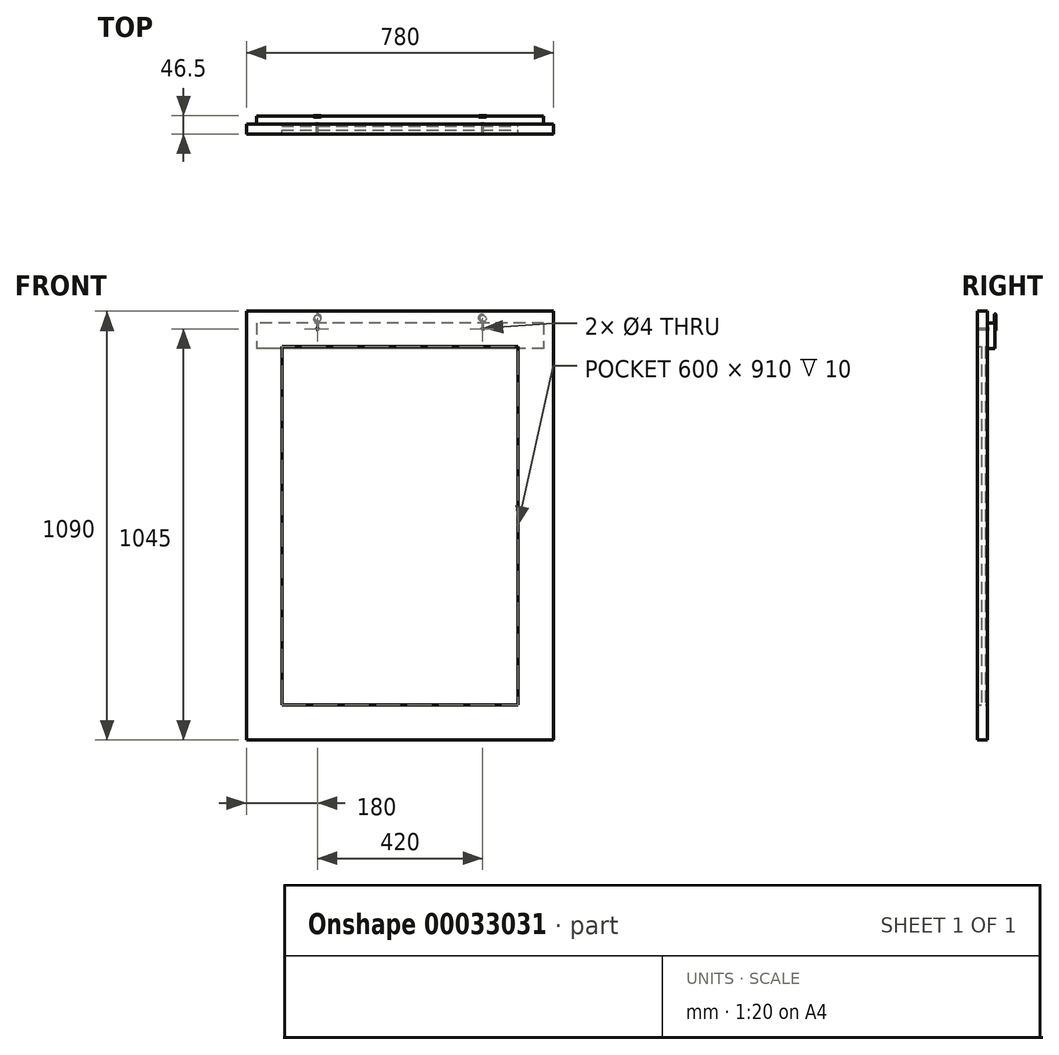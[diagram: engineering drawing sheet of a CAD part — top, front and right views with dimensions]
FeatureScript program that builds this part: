
annotation { "Feature Type Name" : "Feature", "Feature Type Description" : "" }
export const myFeature = defineFeature(function(context is Context, id is Id, definition is map)
    precondition{}
    {
        {
            var Q0;
            Q0=qCreatedBy(makeId("Front.planeOp"),FACE);
            var sketch = newSketch(context, id + "F0", { "sketchPlane" : qUnion([Q0])});
            skLineSegment(sketch, "E0.bottom", {"start": v(-390, 0) * mm, "end": v(390, 0) * mm});
            skLineSegment(sketch, "E0.top", {"start": v(-390, -1090) * mm, "end": v(390, -1090) * mm});
            skLineSegment(sketch, "E0.left", {"start": v(-390, 0) * mm, "end": v(-390, -1090) * mm});
            skLineSegment(sketch, "E0.right", {"start": v(390, 0) * mm, "end": v(390, -1090) * mm});
            skLineSegment(sketch, "E1.0", {"start": v(-300, -90) * mm, "end": v(300, -90) * mm});
            skLineSegment(sketch, "E1.1", {"start": v(-300, -90) * mm, "end": v(-300, -1000) * mm});
            skLineSegment(sketch, "E1.2", {"start": v(-300, -1000) * mm, "end": v(300, -1000) * mm});
            skLineSegment(sketch, "E1.3", {"start": v(300, -90) * mm, "end": v(300, -1000) * mm});
            skSolve(sketch);
        }
        {
            var Q0;
            Q0 = qSketchRegion(id + "F0", true);
            extrude(context, id + "F1", {"entities" : qUnion([Q0]), "depth" : 25 * mm});
        }
        {
            var Q0;
            Q0=qCreatedBy(makeId("Front.planeOp"),FACE);
            cPlane(context, id + "F2", {"entities" : qUnion([Q0]), "cplaneType" : CPlaneType.OFFSET, "offset" : 5 * mm, "width" : 150 * mm, "height" : 150 * mm});
        }
        {
            var Q0;
            Q0=qCreatedBy(id+"F2.planeOp",FACE);
            var sketch = newSketch(context, id + "F3", { "sketchPlane" : qUnion([Q0])});
            skLineSegment(sketch, "E2.0", {"start": v(-300, -90) * mm, "end": v(300, -90) * mm});
            skLineSegment(sketch, "E2.1", {"start": v(-300, -90) * mm, "end": v(-300, -1000) * mm});
            skLineSegment(sketch, "E2.2", {"start": v(-300, -1000) * mm, "end": v(300, -1000) * mm});
            skLineSegment(sketch, "E2.3", {"start": v(300, -90) * mm, "end": v(300, -1000) * mm});
            skSolve(sketch);
        }
        {
            var Q0;
            Q0 = qSketchRegion(id + "F3", true);
            extrude(context, id + "F4", {"entities" : qUnion([Q0]), "operationType" : NewBodyOperationType.ADD, "depth" : 10 * mm});
        }
        {
            var Q0;
            Q0=makeQuery(id+"F1.opExtrude","CAP_FACE",FACE,{"disambiguationData":[OSD([sQuery(id+"F0.wireOp",EDGE,"E0.bottom"),sQuery(id+"F0.wireOp",EDGE,"E0.top"),sQuery(id+"F0.wireOp",EDGE,"E0.left"),sQuery(id+"F0.wireOp",EDGE,"E0.right"),sQuery(id+"F0.wireOp",EDGE,"E1.0"),sQuery(id+"F0.wireOp",EDGE,"E1.1"),sQuery(id+"F0.wireOp",EDGE,"E1.2"),sQuery(id+"F0.wireOp",EDGE,"E1.3")])],"isStart":true});
            var sketch = newSketch(context, id + "F5", { "sketchPlane" : qUnion([Q0])});
            skLineSegment(sketch, "E3.bottom", {"start": v(-365, -30) * mm, "end": v(365, -30) * mm});
            skLineSegment(sketch, "E3.top", {"start": v(-365, -95) * mm, "end": v(365, -95) * mm});
            skLineSegment(sketch, "E3.left", {"start": v(-365, -30) * mm, "end": v(-365, -95) * mm});
            skLineSegment(sketch, "E3.right", {"start": v(365, -30) * mm, "end": v(365, -95) * mm});
            skPoint(sketch, "E4", {"position": v(0, -30) * mm});
            skSolve(sketch);
        }
        {
            var Q0;
            Q0 = qSketchRegion(id + "F5", true);
            extrude(context, id + "F6", {"entities" : qUnion([Q0]), "operationType" : NewBodyOperationType.ADD, "depth" : 20 * mm});
        }
        {
            var Q0;
            Q0=makeQuery(id+"F6.opExtrude","CAP_FACE",FACE,{"disambiguationData":[OSD([sQuery(id+"F5.wireOp",EDGE,"E3.bottom"),sQuery(id+"F5.wireOp",EDGE,"E3.top"),sQuery(id+"F5.wireOp",EDGE,"E3.left"),sQuery(id+"F5.wireOp",EDGE,"E3.right")])],"isStart":false});
            var sketch = newSketch(context, id + "F7", { "sketchPlane" : qUnion([Q0])});
            skCircle(sketch, "E5", {"center": v(210, -45) * mm, "radius": 2 * mm});
            skCircle(sketch, "E6.1.0.0", {"center": v(-210, -45) * mm, "radius": 2 * mm});
            skLineSegment(sketch, "E6.direction1", {"start": v(210, -45) * mm, "end": v(-210, -45) * mm, "construction": true});
            skLineSegment(sketch, "E7", {"start": v(0, -45) * mm, "end": v(0, -30) * mm, "construction": true});
            skSolve(sketch);
        }
        {
            var Q0;
            Q0 = qSketchRegion(id + "F7", true);
            extrude(context, id + "F8", {"entities" : qUnion([Q0]), "operationType" : NewBodyOperationType.REMOVE, "endBound" : BoundingType.UP_TO_NEXT, "oppositeDirection" : true, "depth" : 25 * mm});
        }
        {
            var Q0;
            Q0=sQuery(id+"F7.wireOp",VERTEX,"E6.direction1.start");
            var Q1;
            Q1=makeQuery(id+"F6.opExtrude","CAP_FACE",FACE,{"disambiguationData":[OSD([sQuery(id+"F5.wireOp",EDGE,"E3.bottom"),sQuery(id+"F5.wireOp",EDGE,"E3.top"),sQuery(id+"F5.wireOp",EDGE,"E3.left"),sQuery(id+"F5.wireOp",EDGE,"E3.right")])],"isStart":false});
            cPlane(context, id + "F9", {"entities" : qUnion([Q0, Q1]), "cplaneType" : CPlaneType.PLANE_POINT, "offset" : 150 * mm, "width" : 150 * mm, "height" : 150 * mm});
        }
        {
            var Q0;
            Q0=qCreatedBy(id+"F9.planeOp",FACE);
            var sketch = newSketch(context, id + "F10", { "sketchPlane" : qUnion([Q0])});
            skLineSegment(sketch, "E8", {"start": v(210, -49) * mm, "end": v(210, -29) * mm});
            skArc(sketch, "E9", {"start": v(210, -29) * mm, "mid": v(209.25, -26.67) * mm, "end": v(207.28, -25.21) * mm});
            skArc(sketch, "E10", {"start": v(213, -25.11) * mm, "mid": v(209.85, -8.66) * mm, "end": v(207.28, -25.21) * mm});
            skSolve(sketch);
        }
        {
            var Q0;
            Q0=sQuery(id+"F10.wireOp",VERTEX,"E10.start");
            var Q1;
            Q1=sQuery(id+"F10.wireOp",EDGE,"E10");
            cPlane(context, id + "F11", {"entities" : qUnion([Q0, Q1]), "cplaneType" : CPlaneType.CURVE_POINT, "offset" : 150 * mm, "width" : 150 * mm, "height" : 150 * mm});
        }
        {
            var Q0;
            Q0=qCreatedBy(id+"F11.planeOp",FACE);
            var sketch = newSketch(context, id + "F12", { "sketchPlane" : qUnion([Q0])});
            skCircle(sketch, "E11", {"center": v(-20, -98.67) * mm, "radius": 1.5 * mm});
            skSolve(sketch);
        }
        {
            var Q0;
            Q0 = qSketchRegion(id + "F12", true);
            var Q1;
            Q1 = qConstructionFilter(qBodyType(qCreatedBy(id + "F10" ,EDGE), BodyType.WIRE), ConstructionObject.NO);
            sweep(context, id + "F13", {"profiles" : qUnion([Q0]), "path" : qUnion([Q1])});
        }
        {
            var Q0;
            Q0=makeQuery(id+"F13.opSweep","SWEPT_BODY",BODY,{"disambiguationData":[OSD([sQuery(id+"F10.wireOp",EDGE,"E10"),sQuery(id+"F12.wireOp",EDGE,"E11")])]});
            var Q1;
            Q1=qCreatedBy(makeId("Right.planeOp"),FACE);
            mirror(context, id + "F14", {"entities" : qUnion([Q0]), "mirrorPlane" : qUnion([Q1])});
        }
    });
